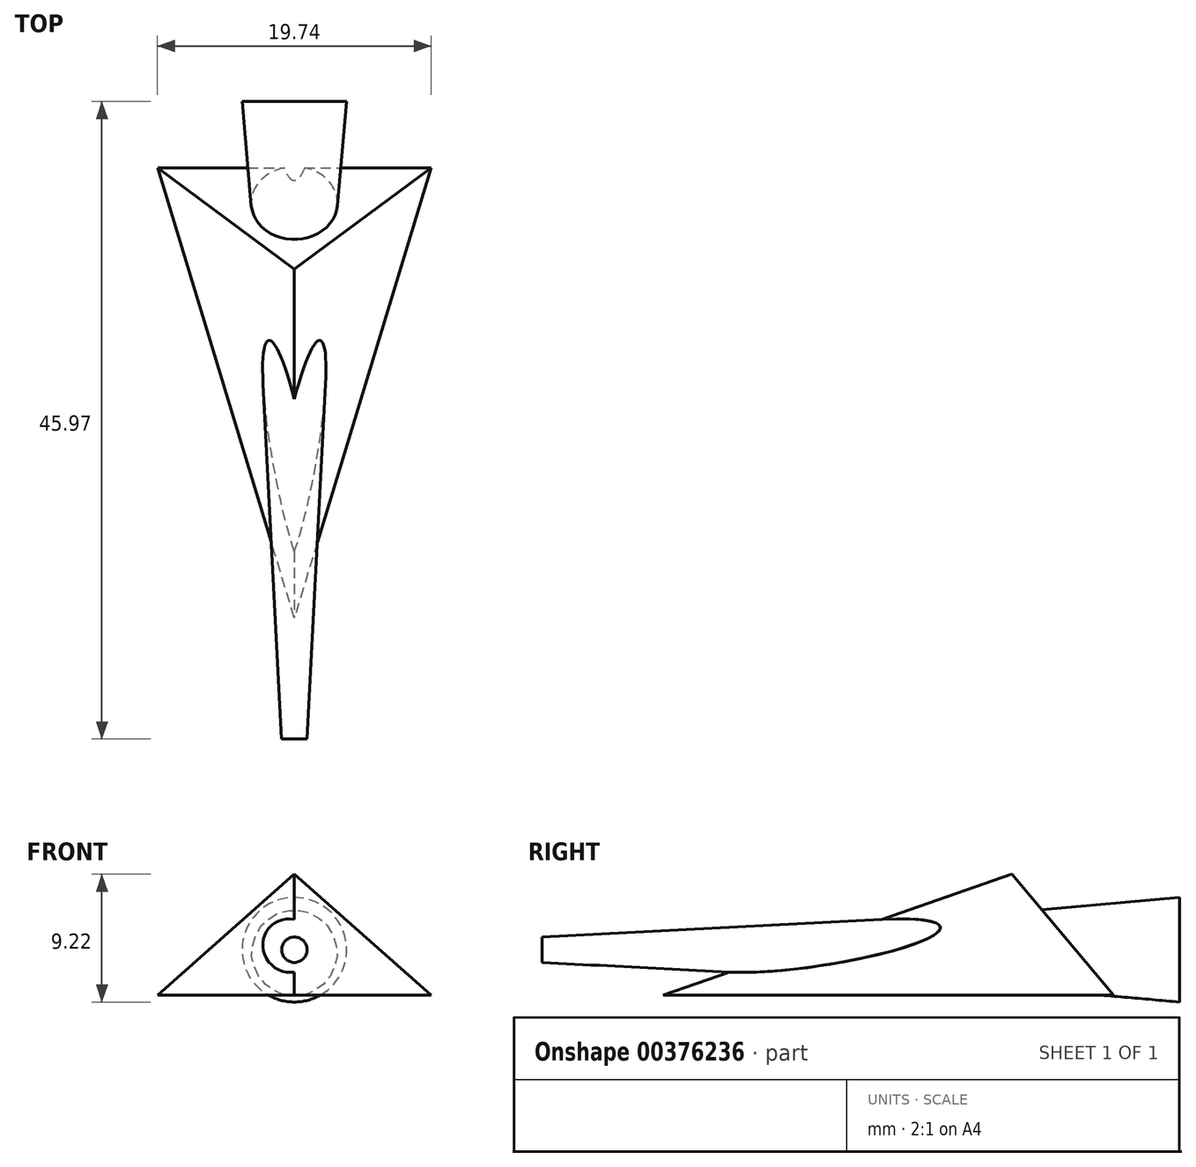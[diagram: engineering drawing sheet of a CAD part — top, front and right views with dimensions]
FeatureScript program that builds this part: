
annotation { "Feature Type Name" : "Feature", "Feature Type Description" : "" }
export const myFeature = defineFeature(function(context is Context, id is Id, definition is map)
    precondition{}
    {
        {
            var Q0;
            Q0=qCreatedBy(makeId("Top.planeOp"),FACE);
            var sketch = newSketch(context, id + "F0", { "sketchPlane" : qUnion([Q0])});
            skLineSegment(sketch, "E0", {"start": v(0, -38.4) * mm, "end": v(-19.74, 26.51) * mm});
            skLineSegment(sketch, "E1", {"start": v(-19.74, 26.51) * mm, "end": v(19.74, 26.51) * mm});
            skLineSegment(sketch, "E2", {"start": v(19.74, 26.51) * mm, "end": v(0, -38.4) * mm});
            skSolve(sketch);
        }
        {
            var Q0;
            Q0=makeQuery(id+"F0.imprint","IMPRINT",FACE,{"disambiguationData":[TD([[makeQuery(id+"F0.imprint","IMPRINT",EDGE,{"derivedFrom":sQuery(id+"F0.wireOp",EDGE,"E0")}),-1.0]])]});
            extrude(context, id + "F1", {"entities" : qUnion([Q0]), "depth" : 25.4 * mm, "hasDraft" : true, "draftAngle" : 40 * degree, "draftPullDirection" : true});
        }
        {
            var Q0;
            Q0=qCreatedBy(makeId("Front.planeOp"),FACE);
            cPlane(context, id + "F2", {"entities" : qUnion([Q0]), "cplaneType" : CPlaneType.OFFSET, "offset" : 10.67 * mm, "oppositeDirection" : true, "width" : 152.4 * mm, "height" : 152.4 * mm});
        }
        {
            var Q0;
            Q0=qCreatedBy(id+"F2.planeOp",FACE);
            var sketch = newSketch(context, id + "F3", { "sketchPlane" : qUnion([Q0])});
            skCircle(sketch, "E3", {"center": v(0, 6.54) * mm, "radius": 5.32 * mm});
            skSolve(sketch);
        }
        {
            var Q0;
            Q0 = qSketchRegion(id + "F3", true);
            extrude(context, id + "F4", {"entities" : qUnion([Q0]), "operationType" : NewBodyOperationType.ADD, "depth" : 66.55 * mm, "hasDraft" : true, "draftAngle" : 3 * degree, "draftPullDirection" : true, "hasSecondDirection" : true, "secondDirectionOppositeDirection" : true, "secondDirectionDepth" : 25.4 * mm, "hasSecondDirectionDraft" : true, "secondDirectionDraftAngle" : 5 * degree});
        }
        {
            var Q0;
            Q0=makeQuery(id+"F1.opExtrude","SWEPT_BODY",BODY,{"disambiguationData":[OSD([sQuery(id+"F0.wireOp",EDGE,"E0"),sQuery(id+"F0.wireOp",EDGE,"E1"),sQuery(id+"F0.wireOp",EDGE,"E2")])]});
            var Q1;
            Q1=qCreatedBy(makeId("Origin.pointOp"),VERTEX);
            transform(context, id + "F5", {"entities" : qUnion([Q0]), "transformType" : TransformType.SCALE_UNIFORMLY, "scale" : .5, "scalePoint" : qUnion([Q1]), "makeCopy" : false});
        }
    });
